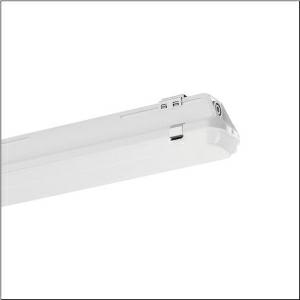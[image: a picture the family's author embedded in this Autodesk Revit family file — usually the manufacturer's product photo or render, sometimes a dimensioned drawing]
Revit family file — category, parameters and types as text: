
# Revit family: monsun_r__21_emergency_51fb20dl447k3h_3ee9
name_source: partatom
category: Lighting Fixtures
units: mm (PartAtom-declared; Revit-internal decimal feet)

## family parameters
Cut with Voids When Loaded = No
Host = Face
Light Source = No
Part Type = Normal
Room Calculation Point = No
Round Connector Dimension = Use Diameter
Shared = No

## types (1)
- --- (1 x LED, 840 lm, 6.2 W, 4000K)
    Apparent Load = 6 VA
    CIE Flux Codes = 45 75 93 94 100
    Color Rendering = 80
    Color Temperature = 4000K
    Default Elevation = 1800 mm
    Description = Monsun® 21 emergency, damp-proof luminaire, chain hanger, primary optical cover: enclosure, of PC, light emission: direct distribution, primary light characteristic: symmetric, installation type: vertical mounting, horizontal mounting, surface-mounted, suspended mounting, LED, rated luminous flux: 4.320lm, luminous efficacy: 162lm/W, light colour: 840, colour temperature: 4000K, control gear: DALI 2, with terminal, 5-pole, max. 2.5mm², mains connection: 220..240V, AC, 50/60Hz, rated input power: 30W, control gear: single battery element, battery: LiFePO4, 9Ah, housing, of glass-fibre reinforced plastic, uncoated, bright grey, incl. chain hanger, length: 1.299mm, width: 90mm, height: 88mm, clip for enclosure, of stainless steel (V2A), ceiling mounting element, of stainless steel (V2A), chain hanger, of stainless steel (V2A), protection rating (complete): IP66, insulation class (complete): insulation class I (protective earthing), certification: CE, UKCA, protection symbol: D, impact resistance: IK08, permissible operating ambient temperature: +5..+25°C, standard: EN 50419, EN 60598-2-1, corresponds to IFS (International Featured Standards) requirements for safety and quality in the food industry, for indoor or canopied outdoor use, no direct snow, no direct sun, no direct rain, LABS conformity tested according to VDMA 24364:2018-05, contact your sales advisor before using the luminaires in applications with unclear chemical exposure, large temperature fluctuations or condensation-forming humidity, packaging unit: 1 piece
    Height = 88 mm
    Lamp = 1 x LED
    Lamp Light Flux = 840 lm
    Lamp Power = 6.2 W
    Lamp count = 1
    Length = 1299 mm
    Luminous efficacy = 135 lm/W
    Manufacturer = Siteco
    ModVariant = No
    Model = 51FB20DL447K3H
    Mounting Place = Ceiling
    Mounting Type = Surface mounted
    Number of Poles = 1
    OnlyDefault = Yes
    Power Factor = 1
    Product Name = Monsun® 21 emergency
    Product group = damp-proof luminaire
    ProductGroupID = 301
    Protection Class = Protection class I
    Protection Degree = IP 66
    RLX_Detail_Level = 1
    RLX_Emergency_Light_Flux = 0 lm
    RLX_Emergency_Type = 0
    RLX_Emergency_Type_DB = No
    RlxData = <blob elided: 94053 chars, md5=38817f35>
    Socket = socket
    Standby Power = 0 W
    System Light Flux = 840 lm
    System Power = 6 W
    Type Comments = : 3 h
    Type Image = l_1319656.jpg
    URL = http://relux.com
    VarID = @adj_042279
    Voltage = 0 V
    Weight = 0.00 kg
    Width = 90 mm

## geometry (parser evidence)
native form markers: Blend x4, Sweep x14
no freeform markers — native parametric forms only
